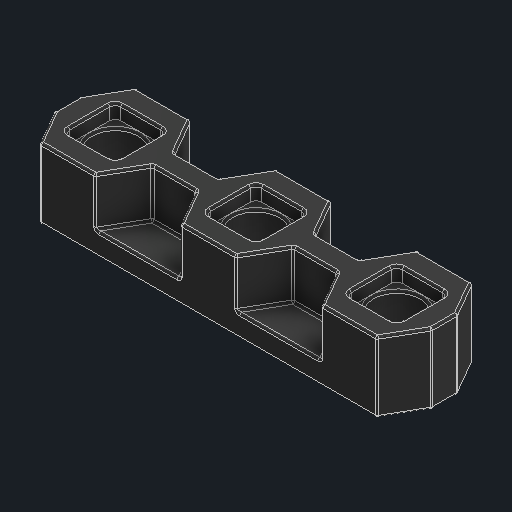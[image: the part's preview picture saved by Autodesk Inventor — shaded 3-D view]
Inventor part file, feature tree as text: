
AUTODESK INVENTOR PART (.ipt)
format: ipt  version: 2025 (Build 290162000, 162)  size: 501,248 bytes
history: native  units: in
note: dims shown in document units (in); Inventor stores cm internally (conversion verified against a paired STEP export)
features: other x3, sketch x1
ambient origin geometry x8: Origin, YZ Plane, XZ Plane, XY Plane, X Axis, Y Axis, Z Axis, Center Point
bodies: Solid1 (feature_tree)
feature tree (4):
  other  "Bearing Flat Low Profile.ipt"
  other  "Solid1::Bearing Flat Low Profile.ipt"
  other  "TaggingFeature1"
  sketch  "Sketch1"  dims[d0=0.3937in]
